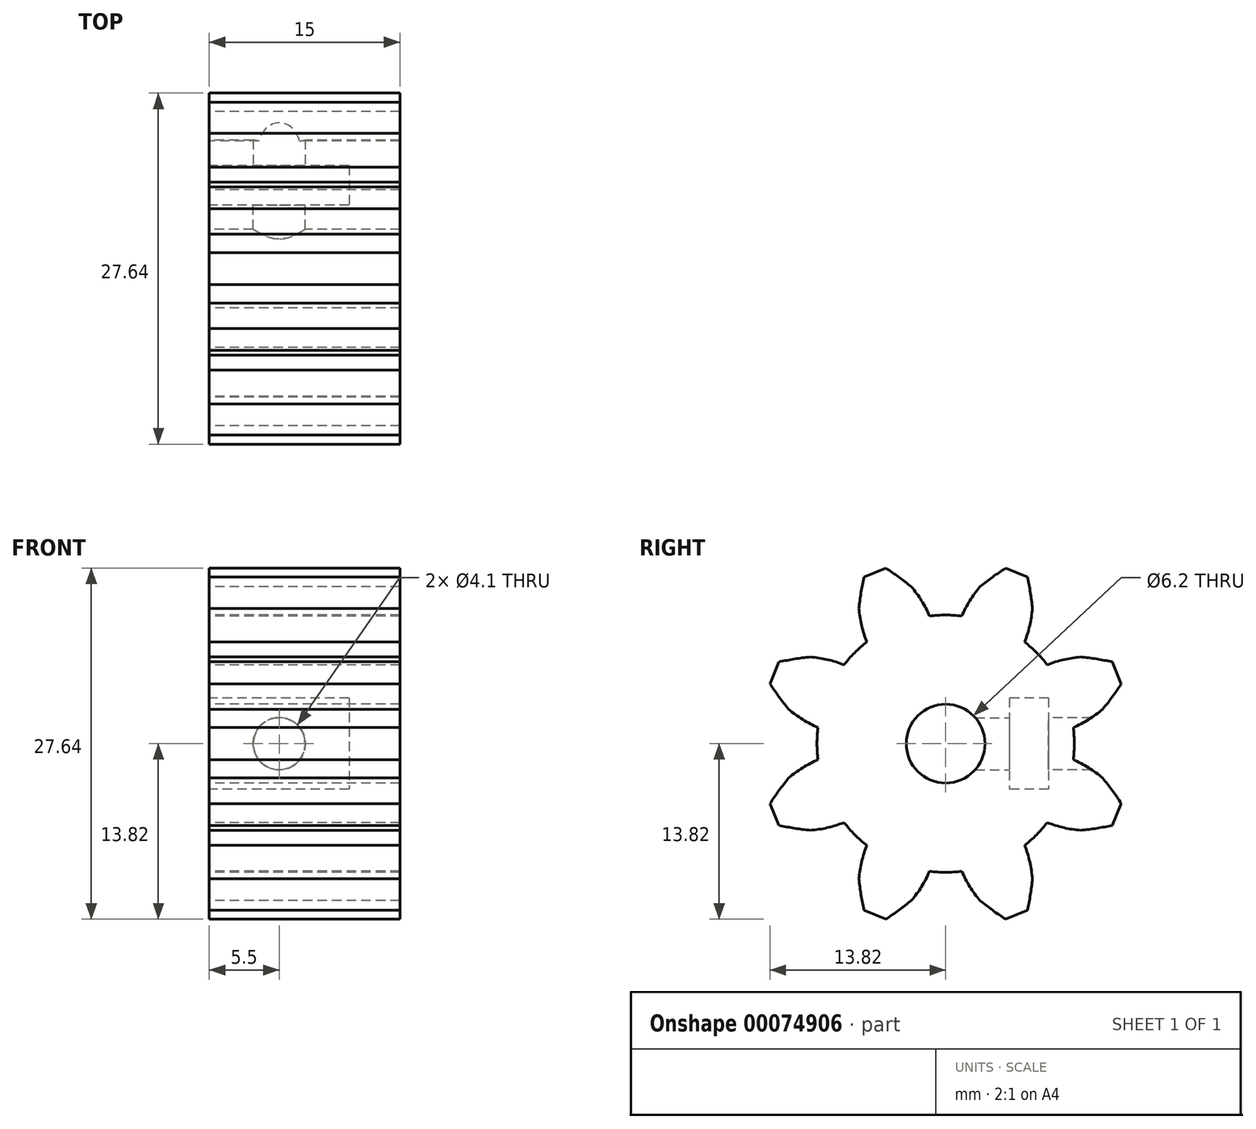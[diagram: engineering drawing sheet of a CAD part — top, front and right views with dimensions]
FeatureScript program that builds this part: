
annotation { "Feature Type Name" : "Feature", "Feature Type Description" : "" }
export const myFeature = defineFeature(function(context is Context, id is Id, definition is map)
    precondition{}
    {
        {
            var Q0;
            Q0=qCreatedBy(makeId("Right.planeOp"),FACE);
            var sketch = newSketch(context, id + "F0", { "sketchPlane" : qUnion([Q0])});
            skCircle(sketch, "E0", {"center": v(0, 0) * mm, "radius": 3.1 * mm});
            skLineSegment(sketch, "E1.bottom", {"start": v(8.1, 3.6) * mm, "end": v(5, 3.6) * mm});
            skLineSegment(sketch, "E1.top", {"start": v(8.1, -3.6) * mm, "end": v(5, -3.6) * mm});
            skLineSegment(sketch, "E1.left", {"start": v(8.1, 3.6) * mm, "end": v(8.1, -3.6) * mm});
            skLineSegment(sketch, "E1.right", {"start": v(5, 3.6) * mm, "end": v(5, -3.6) * mm});
            skPoint(sketch, "E1.middle", {"position": v(6.55, 0) * mm});
            skArc(sketch, "E2", {"start": v(1.27, 10.04) * mm, "mid": v(0, 10.12) * mm, "end": v(-1.27, 10.04) * mm});
            skLineSegment(sketch, "E3", {"start": v(4.72, 13.82) * mm, "end": v(6.43, 13.1) * mm});
            skPoint(sketch, "E4", {"position": v(5.58, 13.46) * mm});
            skLineSegment(sketch, "E5", {"start": v(0, 0) * mm, "end": v(5.58, 13.46) * mm, "construction": true});
            skArc(sketch, "E6", {"start": v(6.43, 13.1) * mm, "mid": v(6.66, 11.88) * mm, "end": v(6.82, 10.65) * mm});
            skArc(sketch, "E7", {"start": v(6.82, 10.65) * mm, "mid": v(6.61, 9.3) * mm, "end": v(6.2, 8) * mm});
            skArc(sketch, "E8", {"start": v(1.27, 10.04) * mm, "mid": v(1.9, 11.25) * mm, "end": v(2.7, 12.35) * mm});
            skArc(sketch, "E9", {"start": v(4.72, 13.82) * mm, "mid": v(3.7, 13.11) * mm, "end": v(2.7, 12.35) * mm});
            skArc(sketch, "E10.1.0", {"start": v(-2.7, 12.35) * mm, "mid": v(-1.9, 11.25) * mm, "end": v(-1.27, 10.04) * mm});
            skArc(sketch, "E10.1.1", {"start": v(-4.72, 13.82) * mm, "mid": v(-3.7, 13.11) * mm, "end": v(-2.7, 12.35) * mm});
            skLineSegment(sketch, "E10.1.2", {"start": v(-6.43, 13.1) * mm, "end": v(-4.72, 13.82) * mm});
            skArc(sketch, "E10.1.3", {"start": v(-6.43, 13.1) * mm, "mid": v(-6.66, 11.88) * mm, "end": v(-6.82, 10.65) * mm});
            skArc(sketch, "E10.1.4", {"start": v(-6.2, 8) * mm, "mid": v(-6.61, 9.3) * mm, "end": v(-6.82, 10.65) * mm});
            skArc(sketch, "E10.2.0", {"start": v(-10.65, 6.82) * mm, "mid": v(-9.3, 6.61) * mm, "end": v(-8, 6.2) * mm});
            skArc(sketch, "E10.2.1", {"start": v(-13.1, 6.43) * mm, "mid": v(-11.88, 6.66) * mm, "end": v(-10.65, 6.82) * mm});
            skLineSegment(sketch, "E10.2.2", {"start": v(-13.82, 4.72) * mm, "end": v(-13.1, 6.43) * mm});
            skArc(sketch, "E10.2.3", {"start": v(-13.82, 4.72) * mm, "mid": v(-13.11, 3.7) * mm, "end": v(-12.35, 2.7) * mm});
            skArc(sketch, "E10.2.4", {"start": v(-10.04, 1.27) * mm, "mid": v(-11.25, 1.9) * mm, "end": v(-12.35, 2.7) * mm});
            skArc(sketch, "E10.3.0", {"start": v(-12.35, -2.7) * mm, "mid": v(-11.25, -1.9) * mm, "end": v(-10.04, -1.27) * mm});
            skArc(sketch, "E10.3.1", {"start": v(-13.82, -4.72) * mm, "mid": v(-13.11, -3.7) * mm, "end": v(-12.35, -2.7) * mm});
            skLineSegment(sketch, "E10.3.2", {"start": v(-13.1, -6.43) * mm, "end": v(-13.82, -4.72) * mm});
            skArc(sketch, "E10.3.3", {"start": v(-13.1, -6.43) * mm, "mid": v(-11.88, -6.66) * mm, "end": v(-10.65, -6.82) * mm});
            skArc(sketch, "E10.3.4", {"start": v(-8, -6.2) * mm, "mid": v(-9.3, -6.61) * mm, "end": v(-10.65, -6.82) * mm});
            skArc(sketch, "E10.4.0", {"start": v(-6.82, -10.65) * mm, "mid": v(-6.61, -9.3) * mm, "end": v(-6.2, -8) * mm});
            skArc(sketch, "E10.4.1", {"start": v(-6.43, -13.1) * mm, "mid": v(-6.66, -11.88) * mm, "end": v(-6.82, -10.65) * mm});
            skLineSegment(sketch, "E10.4.2", {"start": v(-4.72, -13.82) * mm, "end": v(-6.43, -13.1) * mm});
            skArc(sketch, "E10.4.3", {"start": v(-4.72, -13.82) * mm, "mid": v(-3.7, -13.11) * mm, "end": v(-2.7, -12.35) * mm});
            skArc(sketch, "E10.4.4", {"start": v(-1.27, -10.04) * mm, "mid": v(-1.9, -11.25) * mm, "end": v(-2.7, -12.35) * mm});
            skArc(sketch, "E10.5.0", {"start": v(2.7, -12.35) * mm, "mid": v(1.9, -11.25) * mm, "end": v(1.27, -10.04) * mm});
            skArc(sketch, "E10.5.1", {"start": v(4.72, -13.82) * mm, "mid": v(3.7, -13.11) * mm, "end": v(2.7, -12.35) * mm});
            skLineSegment(sketch, "E10.5.2", {"start": v(6.43, -13.1) * mm, "end": v(4.72, -13.82) * mm});
            skArc(sketch, "E10.5.3", {"start": v(6.43, -13.1) * mm, "mid": v(6.66, -11.88) * mm, "end": v(6.82, -10.65) * mm});
            skArc(sketch, "E10.5.4", {"start": v(6.2, -8) * mm, "mid": v(6.61, -9.3) * mm, "end": v(6.82, -10.65) * mm});
            skArc(sketch, "E10.6.0", {"start": v(10.65, -6.82) * mm, "mid": v(9.3, -6.61) * mm, "end": v(8, -6.2) * mm});
            skArc(sketch, "E10.6.1", {"start": v(13.1, -6.43) * mm, "mid": v(11.88, -6.66) * mm, "end": v(10.65, -6.82) * mm});
            skLineSegment(sketch, "E10.6.2", {"start": v(13.82, -4.72) * mm, "end": v(13.1, -6.43) * mm});
            skArc(sketch, "E10.6.3", {"start": v(13.82, -4.72) * mm, "mid": v(13.11, -3.7) * mm, "end": v(12.35, -2.7) * mm});
            skArc(sketch, "E10.6.4", {"start": v(10.04, -1.27) * mm, "mid": v(11.25, -1.9) * mm, "end": v(12.35, -2.7) * mm});
            skArc(sketch, "E10.7.0", {"start": v(12.35, 2.7) * mm, "mid": v(11.25, 1.9) * mm, "end": v(10.04, 1.27) * mm});
            skArc(sketch, "E10.7.1", {"start": v(13.82, 4.72) * mm, "mid": v(13.11, 3.7) * mm, "end": v(12.35, 2.7) * mm});
            skLineSegment(sketch, "E10.7.2", {"start": v(13.1, 6.43) * mm, "end": v(13.82, 4.72) * mm});
            skArc(sketch, "E10.7.3", {"start": v(13.1, 6.43) * mm, "mid": v(11.88, 6.66) * mm, "end": v(10.65, 6.82) * mm});
            skArc(sketch, "E10.7.4", {"start": v(8, 6.2) * mm, "mid": v(9.3, 6.61) * mm, "end": v(10.65, 6.82) * mm});
            skArc(sketch, "E11.trimOffspring", {"start": v(-6.2, 8) * mm, "mid": v(-7.16, 7.16) * mm, "end": v(-8, 6.2) * mm});
            skArc(sketch, "E12.trimOffspring", {"start": v(-10.04, 1.27) * mm, "mid": v(-10.12, 0) * mm, "end": v(-10.04, -1.27) * mm});
            skArc(sketch, "E13.trimOffspring", {"start": v(6.2, -8) * mm, "mid": v(7.16, -7.16) * mm, "end": v(8, -6.2) * mm});
            skArc(sketch, "E14.trimOffspring", {"start": v(-1.27, -10.04) * mm, "mid": v(0, -10.12) * mm, "end": v(1.27, -10.04) * mm});
            skArc(sketch, "E15.trimOffspring", {"start": v(-8, -6.2) * mm, "mid": v(-7.16, -7.16) * mm, "end": v(-6.2, -8) * mm});
            skArc(sketch, "E16.trimOffspring", {"start": v(10.04, -1.27) * mm, "mid": v(10.12, 0) * mm, "end": v(10.04, 1.27) * mm});
            skArc(sketch, "E17.trimOffspring", {"start": v(8, 6.2) * mm, "mid": v(7.16, 7.16) * mm, "end": v(6.2, 8) * mm});
            skSolve(sketch);
        }
        {
            var Q0;
            Q0=makeQuery(id+"F0.imprint","IMPRINT",FACE,{"disambiguationData":[TD([[makeQuery(id+"F0.imprint","IMPRINT",EDGE,{"derivedFrom":sQuery(id+"F0.wireOp",EDGE,"E0")}),-1.0]])]});
            var Q1;
            Q1=makeQuery(id+"F0.imprint","IMPRINT",FACE,{"disambiguationData":[TD([[makeQuery(id+"F0.imprint","IMPRINT",EDGE,{"derivedFrom":sQuery(id+"F0.wireOp",EDGE,"E1.bottom")}),1.0]])]});
            extrude(context, id + "F1", {"entities" : qUnion([Q0, Q1]), "depth" : 15 * mm});
        }
        {
            var Q0;
            Q0=makeQuery(id+"F0.imprint","IMPRINT",FACE,{"disambiguationData":[TD([[makeQuery(id+"F0.imprint","IMPRINT",EDGE,{"derivedFrom":sQuery(id+"F0.wireOp",EDGE,"E1.bottom")}),1.0]])]});
            extrude(context, id + "F2", {"entities" : qUnion([Q0]), "operationType" : NewBodyOperationType.REMOVE, "depth" : 11 * mm});
        }
        {
            var Q0;
            Q0=makeQuery(id+"F2.boolean.opBoolean","COPY",FACE,{"derivedFrom":makeQuery(id+"F2.opExtrude","SWEPT_FACE",FACE,{"disambiguationData":[OSD([sQuery(id+"F0.wireOp",EDGE,"E1.right")])]})});
            var sketch = newSketch(context, id + "F3", { "sketchPlane" : qUnion([Q0])});
            skLineSegment(sketch, "E18", {"start": v(0, 0) * mm, "end": v(-11, 0) * mm, "construction": true});
            skPoint(sketch, "E19", {"position": v(-5.5, 0) * mm});
            skCircle(sketch, "E20", {"center": v(-5.5, 0) * mm, "radius": 2.05 * mm});
            skSolve(sketch);
        }
        {
            var Q0;
            Q0=makeQuery(id+"F3.imprint","IMPRINT",FACE,{"disambiguationData":[TD([[makeQuery(id+"F3.imprint","IMPRINT",EDGE,{"derivedFrom":sQuery(id+"F3.wireOp",EDGE,"E20")}),1.0]])]});
            extrude(context, id + "F4", {"entities" : qUnion([Q0]), "operationType" : NewBodyOperationType.REMOVE, "oppositeDirection" : true, "depth" : 5 * mm});
        }
        {
            var Q0;
            Q0=makeQuery(id+"F3.imprint","IMPRINT",FACE,{"disambiguationData":[TD([[makeQuery(id+"F3.imprint","IMPRINT",EDGE,{"derivedFrom":sQuery(id+"F3.wireOp",EDGE,"E20")}),1.0]])]});
            extrude(context, id + "F5", {"entities" : qUnion([Q0]), "operationType" : NewBodyOperationType.REMOVE, "depth" : 25 * mm});
        }
    });
